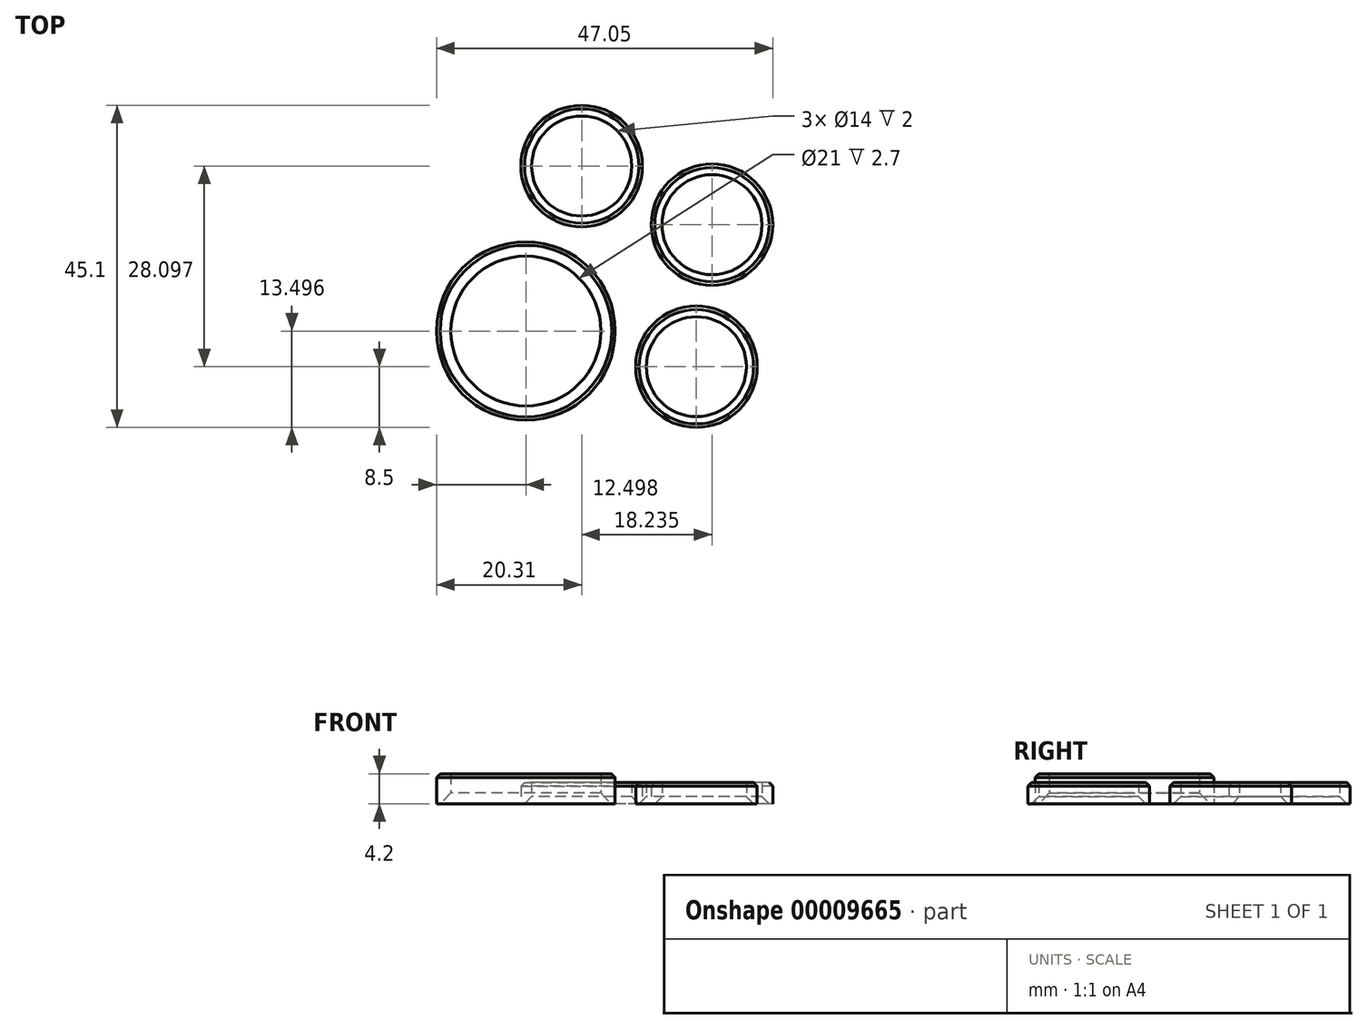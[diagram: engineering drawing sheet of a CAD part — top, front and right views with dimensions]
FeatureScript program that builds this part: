
annotation { "Feature Type Name" : "Feature", "Feature Type Description" : "" }
export const myFeature = defineFeature(function(context is Context, id is Id, definition is map)
    precondition{}
    {
        {
            var Q0;
            Q0=qCreatedBy(makeId("Top.planeOp"),FACE);
            var sketch = newSketch(context, id + "F0", { "sketchPlane" : qUnion([Q0]), "disableImprinting" : false});
            skCircle(sketch, "E0", {"center": v(-28.36, 43.29) * mm, "radius": 12.5 * mm});
            skCircle(sketch, "E1", {"center": v(-4.5, 38.3) * mm, "radius": 8.5 * mm});
            skCircle(sketch, "E2", {"center": v(-2.31, 58.17) * mm, "radius": 8.5 * mm});
            skCircle(sketch, "E3", {"center": v(-20.55, 66.39) * mm, "radius": 8.5 * mm});
            skLineSegment(sketch, "E4", {"start": v(-20.55, 66.39) * mm, "end": v(-2.31, 58.17) * mm, "construction": true});
            skLineSegment(sketch, "E5", {"start": v(-2.31, 58.17) * mm, "end": v(-4.5, 38.3) * mm, "construction": true});
            skLineSegment(sketch, "E6", {"start": v(-28.36, 43.29) * mm, "end": v(-2.31, 58.17) * mm, "construction": true});
            skCircle(sketch, "E7", {"center": v(-17.5, 49.49) * mm, "radius": 27.5 * mm});
            skCircle(sketch, "E8", {"center": v(-28.36, 43.29) * mm, "radius": 10.5 * mm});
            skCircle(sketch, "E9", {"center": v(-2.31, 58.17) * mm, "radius": 7 * mm});
            skCircle(sketch, "E10", {"center": v(-20.55, 66.39) * mm, "radius": 7 * mm});
            skCircle(sketch, "E11", {"center": v(-4.5, 38.3) * mm, "radius": 7 * mm});
            skSolve(sketch);
        }
        {
            var Q0;
            Q0=makeQuery(id+"F0.imprint","IMPRINT",FACE,{"disambiguationData":[TD([[makeQuery(id+"F0.imprint","IMPRINT",EDGE,{"derivedFrom":sQuery(id+"F0.wireOp",EDGE,"E3")}),1.0]])]});
            var Q1;
            Q1=makeQuery(id+"F0.imprint","IMPRINT",FACE,{"disambiguationData":[TD([[makeQuery(id+"F0.imprint","IMPRINT",EDGE,{"derivedFrom":sQuery(id+"F0.wireOp",EDGE,"E2")}),1.0]])]});
            var Q2;
            Q2=makeQuery(id+"F0.imprint","IMPRINT",FACE,{"disambiguationData":[TD([[makeQuery(id+"F0.imprint","IMPRINT",EDGE,{"derivedFrom":sQuery(id+"F0.wireOp",EDGE,"E1")}),1.0]])]});
            extrude(context, id + "F1", {"entities" : qUnion([Q0, Q1, Q2]), "depth" : 3 * mm});
        }
        {
            var Q0;
            Q0=makeQuery(id+"F0.imprint","IMPRINT",FACE,{"disambiguationData":[TD([[makeQuery(id+"F0.imprint","IMPRINT",EDGE,{"derivedFrom":sQuery(id+"F0.wireOp",EDGE,"E0")}),1.0]])]});
            extrude(context, id + "F2", {"entities" : qUnion([Q0]), "depth" : 4.2 * mm});
        }
        {
            var Q0;
            Q0=makeQuery(id+"F1.opExtrude","CAP_EDGE",EDGE,{"disambiguationData":[OSD([sQuery(id+"F0.wireOp",EDGE,"E3")])],"isStart":false});
            var Q1;
            Q1=makeQuery(id+"F1.opExtrude","CAP_EDGE",EDGE,{"disambiguationData":[OSD([sQuery(id+"F0.wireOp",EDGE,"E2")])],"isStart":false});
            var Q2;
            Q2=makeQuery(id+"F1.opExtrude","CAP_EDGE",EDGE,{"disambiguationData":[OSD([sQuery(id+"F0.wireOp",EDGE,"E1")])],"isStart":false});
            chamfer(context, id + "F3", {"entities" : qUnion([Q0, Q1, Q2]), "width" : 0.5 * mm, "tangentPropagation" : true});
        }
        {
            var Q0;
            Q0=makeQuery(id+"F2.opExtrude","CAP_EDGE",EDGE,{"disambiguationData":[OSD([sQuery(id+"F0.wireOp",EDGE,"E0")])],"isStart":false});
            chamfer(context, id + "F4", {"entities" : qUnion([Q0]), "width" : 0.5 * mm, "tangentPropagation" : true});
        }
        {
            var Q0;
            Q0=makeQuery(id+"F1.opExtrude","CAP_EDGE",EDGE,{"disambiguationData":[OSD([sQuery(id+"F0.wireOp",EDGE,"E10")])],"isStart":true});
            var Q1;
            Q1=makeQuery(id+"F1.opExtrude","CAP_EDGE",EDGE,{"disambiguationData":[OSD([sQuery(id+"F0.wireOp",EDGE,"E11")])],"isStart":true});
            var Q2;
            Q2=makeQuery(id+"F1.opExtrude","CAP_EDGE",EDGE,{"disambiguationData":[OSD([sQuery(id+"F0.wireOp",EDGE,"E9")])],"isStart":true});
            chamfer(context, id + "F5", {"entities" : qUnion([Q0, Q1, Q2]), "width" : 1 * mm, "tangentPropagation" : true});
        }
        {
            var Q0;
            Q0=makeQuery(id+"F2.opExtrude","CAP_EDGE",EDGE,{"disambiguationData":[OSD([sQuery(id+"F0.wireOp",EDGE,"E8")])],"isStart":true});
            chamfer(context, id + "F6", {"entities" : qUnion([Q0]), "width" : 1.5 * mm, "tangentPropagation" : true});
        }
    });
